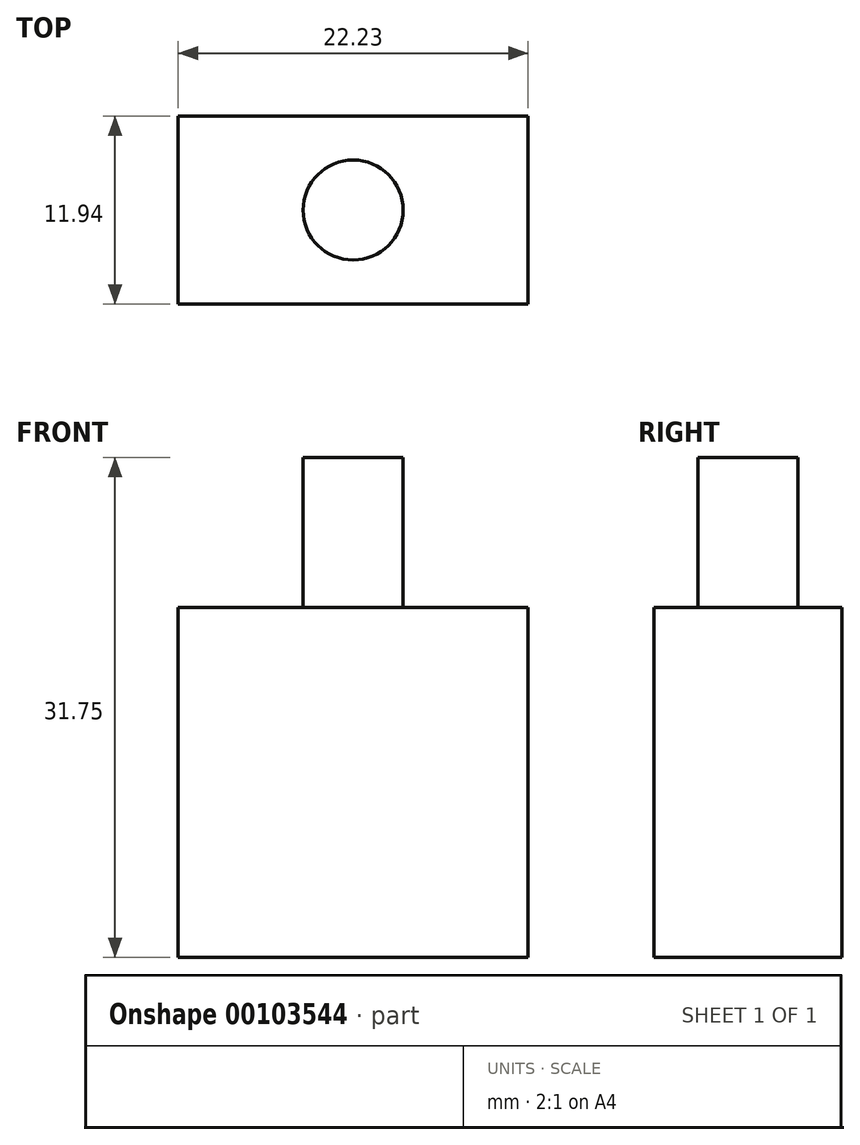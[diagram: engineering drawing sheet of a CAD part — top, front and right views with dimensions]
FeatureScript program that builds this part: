
annotation { "Feature Type Name" : "Feature", "Feature Type Description" : "" }
export const myFeature = defineFeature(function(context is Context, id is Id, definition is map)
    precondition{}
    {
        {
            var Q0;
            Q0=qCreatedBy(makeId("Front.planeOp"),FACE);
            var sketch = newSketch(context, id + "F0", { "sketchPlane" : qUnion([Q0])});
            skLineSegment(sketch, "E0.bottom", {"start": v(-23.1, 25.73) * mm, "end": v(-0.88, 25.73) * mm});
            skLineSegment(sketch, "E0.top", {"start": v(-23.1, 3.5) * mm, "end": v(-0.88, 3.5) * mm});
            skLineSegment(sketch, "E0.left", {"start": v(-23.1, 25.73) * mm, "end": v(-23.1, 3.5) * mm});
            skLineSegment(sketch, "E0.right", {"start": v(-0.88, 25.73) * mm, "end": v(-0.88, 3.5) * mm});
            skSolve(sketch);
        }
        {
            var Q0;
            Q0 = qSketchRegion(id + "F0", true);
            extrude(context, id + "F1", {"entities" : qUnion([Q0]), "depth" : 11.94 * mm});
        }
        {
            var Q0;
            Q0=makeQuery(id+"F1.opExtrude","SWEPT_FACE",FACE,{"disambiguationData":[OSD([sQuery(id+"F0.wireOp",EDGE,"E0.bottom")])]});
            var sketch = newSketch(context, id + "F2", { "sketchPlane" : qUnion([Q0])});
            skCircle(sketch, "E1", {"center": v(-12, -5.97) * mm, "radius": 3.18 * mm});
            skPoint(sketch, "E1.centerSnap0", {"position": v(-0.88, -5.97) * mm});
            skPoint(sketch, "E1.centerSnap1", {"position": v(-12, 0) * mm});
            skSolve(sketch);
        }
        {
            var Q0;
            Q0=makeQuery(id+"F2.imprint","IMPRINT",FACE,{"disambiguationData":[TD([[makeQuery(id+"F2.imprint","IMPRINT",EDGE,{"derivedFrom":sQuery(id+"F2.wireOp",EDGE,"E1")}),1.0]])]});
            extrude(context, id + "F3", {"entities" : qUnion([Q0]), "operationType" : NewBodyOperationType.ADD, "depth" : 9.52 * mm});
        }
    });
